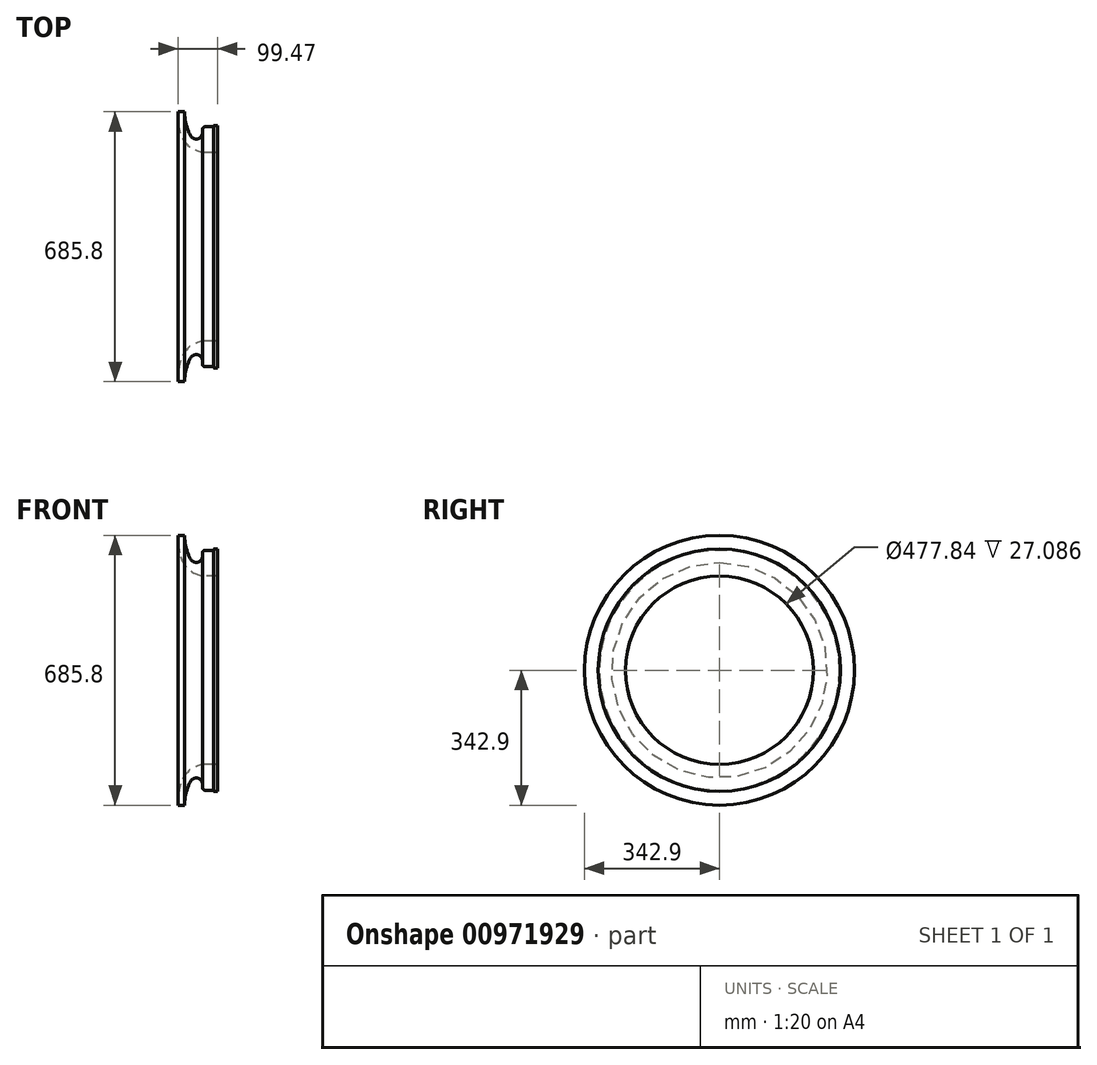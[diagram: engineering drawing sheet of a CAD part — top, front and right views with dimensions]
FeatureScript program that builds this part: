
annotation { "Feature Type Name" : "Feature", "Feature Type Description" : "" }
export const myFeature = defineFeature(function(context is Context, id is Id, definition is map)
    precondition{}
    {
        {
            var Q0;
            Q0=qCreatedBy(makeId("Front.planeOp"),FACE);
            var sketch = newSketch(context, id + "F0", { "sketchPlane" : qUnion([Q0])});
            skLineSegment(sketch, "E0", {"start": v(0, 342.9) * mm, "end": v(15.88, 342.9) * mm});
            skLineSegment(sketch, "E1", {"start": v(99.47, 307.94) * mm, "end": v(99.47, 238.92) * mm});
            skLineSegment(sketch, "E2", {"start": v(99.47, 307.94) * mm, "end": v(89.94, 307.94) * mm});
            skLineSegment(sketch, "E3", {"start": v(88.35, 304.8) * mm, "end": v(67.72, 304.8) * mm});
            skLineSegment(sketch, "E4", {"start": v(89.94, 306.39) * mm, "end": v(89.94, 307.94) * mm});
            skArc(sketch, "E5", {"start": v(0, 328.61) * mm, "mid": v(1.1, 311.1) * mm, "end": v(4.35, 293.86) * mm});
            skLineSegment(sketch, "E6", {"start": v(0, 342.9) * mm, "end": v(0, 328.61) * mm});
            skLineSegment(sketch, "E7", {"start": v(99.47, 238.92) * mm, "end": v(72.38, 238.92) * mm});
            skArc(sketch, "E8", {"start": v(15.88, 342.9) * mm, "mid": v(19.87, 311.5) * mm, "end": v(31.6, 282.08) * mm});
            skLineSegment(sketch, "E9", {"start": v(61.37, 298.45) * mm, "end": v(61.37, 289.78) * mm});
            skPoint(sketch, "E10.visualSharp", {"position": v(61.37, 304.8) * mm});
            skArc(sketch, "E10.filletArc", {"start": v(67.72, 304.8) * mm, "mid": v(63.23, 302.94) * mm, "end": v(61.37, 298.45) * mm});
            skPoint(sketch, "E11.visualSharp", {"position": v(89.94, 304.8) * mm});
            skArc(sketch, "E11.filletArc", {"start": v(88.35, 304.8) * mm, "mid": v(89.48, 305.26) * mm, "end": v(89.94, 306.39) * mm});
            skArc(sketch, "E12", {"start": v(31.6, 282.08) * mm, "mid": v(49.47, 274.41) * mm, "end": v(61.37, 289.78) * mm});
            skLineSegment(sketch, "E13", {"start": v(0, 0) * mm, "end": v(60.94, 0) * mm});
            skArc(sketch, "E14", {"start": v(0, 328.61) * mm, "mid": v(1.45, 308.45) * mm, "end": v(5.77, 288.7) * mm});
            skArc(sketch, "E15", {"start": v(5.77, 288.7) * mm, "mid": v(30.8, 252.74) * mm, "end": v(72.38, 238.92) * mm});
            skSolve(sketch);
        }
        {
            var Q0;
            Q0 = qSketchRegion(id + "F0", true);
            var Q1;
            Q1=sQuery(id+"F0.wireOp",EDGE,"E13");
            revolve(context, id + "F1", {"surfaceOperationType" : NewSurfaceOperationType.NEW, "entities" : qUnion([Q0]), "axis" : qUnion([Q1]), "revolveType" : RevolveType.FULL});
        }
    });
